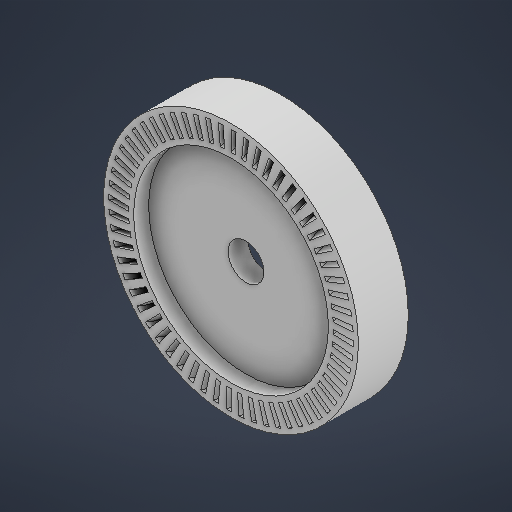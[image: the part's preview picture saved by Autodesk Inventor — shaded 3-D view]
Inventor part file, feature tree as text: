
AUTODESK INVENTOR PART (.ipt)
format: ipt  version: 2025.3 (Build 293356030, 356C)  size: 935,936 bytes
history: native  units: mm
features: extrude x4, sketch x2, plane x1, emboss x1, pattern_circular x1
ambient origin geometry x8: Origin, YZ Plane, XZ Plane, XY Plane, X Axis, Y Axis, Z Axis, Center Point
bodies: Solid1 (feature_tree)
feature tree (9):
  sketch  "Sketch1"  dims[d0=7.2mm d1=41.0mm]
  extrude  "Extrusion1"  Depth=41.0mm
  extrude  "Extrusion3"  Depth=10.0mm
  plane  "Work Plane2"
  emboss  "Emboss1"
  extrude  "Extrusion5"  Depth=10.0mm
  pattern_circular  "Circular Pattern2"  [2 undecoded]
  extrude  "Extrusion6"  Depth=10.0mm TaperAngle=0.0deg
  sketch  "Sketch3"  dims[d2=49.0mm d3=51.0mm d4=39.0mm d5=0.816327mm d6=4.0mm d7=0.0mm d10=10.0mm d11=0.0mm d14=4.5mm d15=0.0mm d21=10.0mm d22=1.0mm d23=1.0mm d24=10.0mm d25=0.0mm d26=600.0mm d27=360.0deg d29=10.0mm d30=0.0mm]
note: 2 required parameter values undecoded (feature->parameter linkage not recoverable at this tier; creation-order binding heuristic only, values carry confidence <= 0.55)
